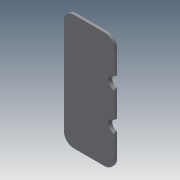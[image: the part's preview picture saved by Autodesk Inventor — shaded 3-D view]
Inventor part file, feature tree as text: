
AUTODESK INVENTOR PART (.ipt)
format: ipt  version: 2013 (Build 170138000, 138)  size: 160,256 bytes
history: native  units: mm
features: extrude x2, fillet x2, sketch x2, chamfer x1
ambient origin geometry x8: Origin, YZ Plane, XZ Plane, XY Plane, X Axis, Y Axis, Z Axis, Center Point
bodies: Solid1 (feature_tree)
feature tree (7):
  extrude  "Extrusion1"  Depth=101.2mm
  fillet  "Fillet1"  Radius=5.0mm
  extrude  "Extrusion2"  Depth=5.0mm TaperAngle=0.0deg
  chamfer  "Chamfer1"  Distance=3.0mm Angle=45.0deg
  fillet  "Fillet2"  Radius=4.0mm
  sketch  "Sketch1"  dims[d0=231.3mm d1=101.2mm d2=5.0mm d3=0.0mm]
  sketch  "Sketch2"  dims[d4=20.0mm d8=5.0mm d9=0.0mm d10=3.0mm d11=2.0mm d12=45.0deg d13=4.0mm]
